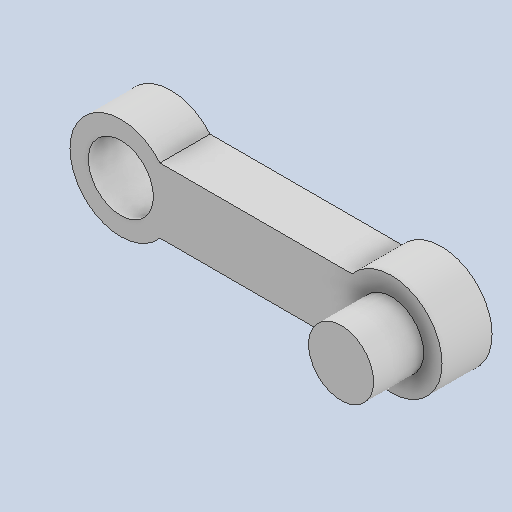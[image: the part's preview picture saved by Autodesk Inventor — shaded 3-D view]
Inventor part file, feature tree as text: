
AUTODESK INVENTOR PART (.ipt)
format: ipt  version: 2022 (Build 260153000, 153)  size: 122,368 bytes
history: native  units: in
note: dims shown in document units (in); Inventor stores cm internally (conversion verified against a paired STEP export)
features: other x3, sketch x1
ambient origin geometry x8: Origin, YZ Plane, XZ Plane, XY Plane, X Axis, Y Axis, Z Axis, Center Point
bodies: Solid1 (feature_tree)
feature tree (4):
  other  "Component32.ipt"
  other  "Solid2::Component32.ipt"
  other  "TaggingFeature1"
  sketch  "Sketch2"  dims[d0=0.3937in]
